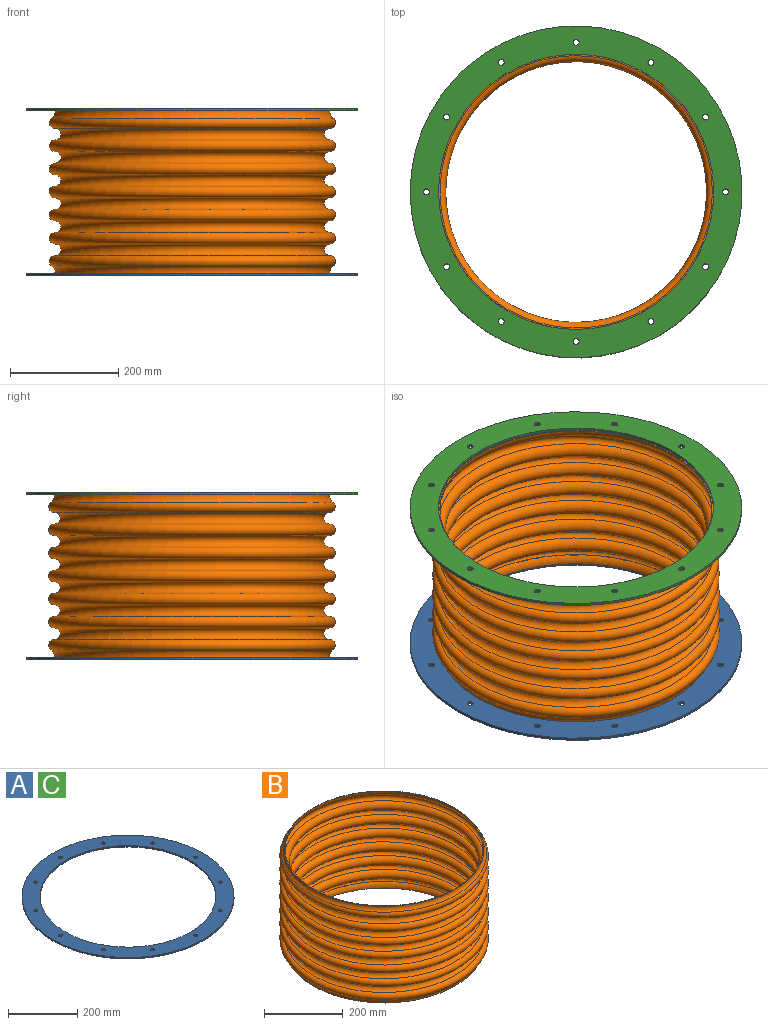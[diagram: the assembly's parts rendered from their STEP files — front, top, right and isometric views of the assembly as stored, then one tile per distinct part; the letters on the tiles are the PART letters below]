
ASSEMBLY  parts=3 mates=1
PART A: 16 faces, bbox 612.8x612.8x4.8 mm
  f0: cylinder r=5.49mm len=10.99mm, axis (0,0,1), area 164.4mm2, adj f14,f15
  f1: cylinder r=5.49mm len=10.99mm, axis (0,0,1), area 164.4mm2, adj f14,f15
  f2: cylinder r=5.49mm len=10.99mm, axis (0,0,1), area 164.4mm2, adj f14,f15
  f3: cylinder r=5.49mm len=10.99mm, axis (0,0,1), area 164.4mm2, adj f14,f15
  f4: cylinder r=5.49mm len=10.99mm, axis (0,0,1), area 164.4mm2, adj f14,f15
  f5: cylinder r=5.49mm len=10.99mm, axis (0,0,1), area 164.4mm2, adj f14,f15
  f6: cylinder r=5.49mm len=10.99mm, axis (0,0,1), area 164.4mm2, adj f14,f15
  f7: cylinder r=5.49mm len=10.99mm, axis (0,0,1), area 164.4mm2, adj f14,f15
  f8: cylinder r=5.49mm len=10.99mm, axis (0,0,1), area 164.4mm2, adj f14,f15
  f9: cylinder r=5.49mm len=10.99mm, axis (0,0,1), area 164.4mm2, adj f14,f15
  f10: cylinder r=5.49mm len=10.99mm, axis (0,0,1), area 164.4mm2, adj f14,f15
  f11: cylinder r=5.49mm len=10.99mm, axis (0,0,1), area 164.4mm2, adj f14,f15
  f12: cylinder r=254mm len=508mm, axis (0,0,1), area 7600.6mm2, adj f14,f15
  f13: cylinder r=306.39mm len=612.78mm, axis (0,0,1), area 9168.2mm2, adj f14,f15
  f14: plane 612.78x612.78mm, normal (0,0,-1), area 91091.3mm2, adj f0,f1,f2,f3,f4,f5,f6,f7
  f15: plane 612.78x612.78mm, normal (0,0,1), area 91091.3mm2, adj f0,f1,f2,f3,f4,f5,f6,f7
PART B: 32 faces, bbox 583.8x583.8x324.4 mm
  f0: plane 508x508mm, normal (0,0,1), area 4037.9mm2, adj f1,f17
  f1: torus R=269.69mm, axis (0,0,1), area 24885.6mm2, adj f0,f2
  f2: torus R=254mm, axis (0,0,1), area 43931.2mm2, adj f1,f3
  f3: torus R=254mm, axis (0,0,1), area 52056.7mm2, adj f2,f4
  f4: torus R=254mm, axis (0,0,1), area 54916.9mm2, adj f3,f5
  f5: torus R=254mm, axis (0,0,1), area 52056.7mm2, adj f4,f6
  f6: torus R=254mm, axis (0,0,1), area 54916.9mm2, adj f5,f7
  f7: torus R=254mm, axis (0,0,1), area 52056.7mm2, adj f6,f8
  f8: torus R=254mm, axis (0,0,1), area 54916.9mm2, adj f7,f16
  f9: plane 508x508mm, normal (0,0,-1), area 4037.9mm2, adj f10,f25
  f10: torus R=269.69mm, axis (0,0,-1), area 24885.6mm2, adj f9,f11
  f11: torus R=254mm, axis (0,0,-1), area 43931.2mm2, adj f10,f12
  f12: torus R=254mm, axis (0,0,-1), area 52056.7mm2, adj f11,f13
  f13: torus R=254mm, axis (0,0,-1), area 54916.9mm2, adj f12,f14
  f14: torus R=254mm, axis (0,0,-1), area 52056.7mm2, adj f13,f15
  f15: torus R=254mm, axis (0,0,-1), area 54916.9mm2, adj f14,f16
  f16: torus R=254mm, axis (0,0,-1), area 52056.7mm2, adj f8,f15
  f17: torus R=269.69mm, axis (0,0,1), area 28456.1mm2, adj f0,f18
  f18: torus R=254mm, axis (0,0,1), area 33237.4mm2, adj f17,f19
  f19: torus R=254mm, axis (0,0,1), area 64029.5mm2, adj f18,f20
  f20: torus R=254mm, axis (0,0,1), area 41582mm2, adj f19,f21
  f21: torus R=254mm, axis (0,0,1), area 64029.5mm2, adj f20,f22
  f22: torus R=254mm, axis (0,0,1), area 41582mm2, adj f21,f23
  f23: torus R=254mm, axis (0,0,1), area 64029.5mm2, adj f22,f24
  f24: torus R=254mm, axis (0,0,1), area 41582mm2, adj f23,f31
  f25: torus R=269.69mm, axis (0,0,-1), area 28456.1mm2, adj f9,f26
  f26: torus R=254mm, axis (0,0,-1), area 33237.4mm2, adj f25,f27
  f27: torus R=254mm, axis (0,0,-1), area 64029.5mm2, adj f26,f28
  f28: torus R=254mm, axis (0,0,-1), area 41582mm2, adj f27,f29
  f29: torus R=254mm, axis (0,0,-1), area 64029.5mm2, adj f28,f30
  f30: torus R=254mm, axis (0,0,-1), area 41582mm2, adj f29,f31
  f31: torus R=254mm, axis (0,0,-1), area 64029.5mm2, adj f24,f30
PART C: same geometry as A
PLACE A t=(-8505.85,14761.09,-9676.46)mm
PLACE B t=(-8505.85,14761.09,-9681.22)mm
PLACE C t=(-8505.85,14761.09,-9371.66)mm
MATE fastened B.f1 <-> A.f12  axis (0,0,-1) through (-7064.4,-9891.02,-9062.86)mm
